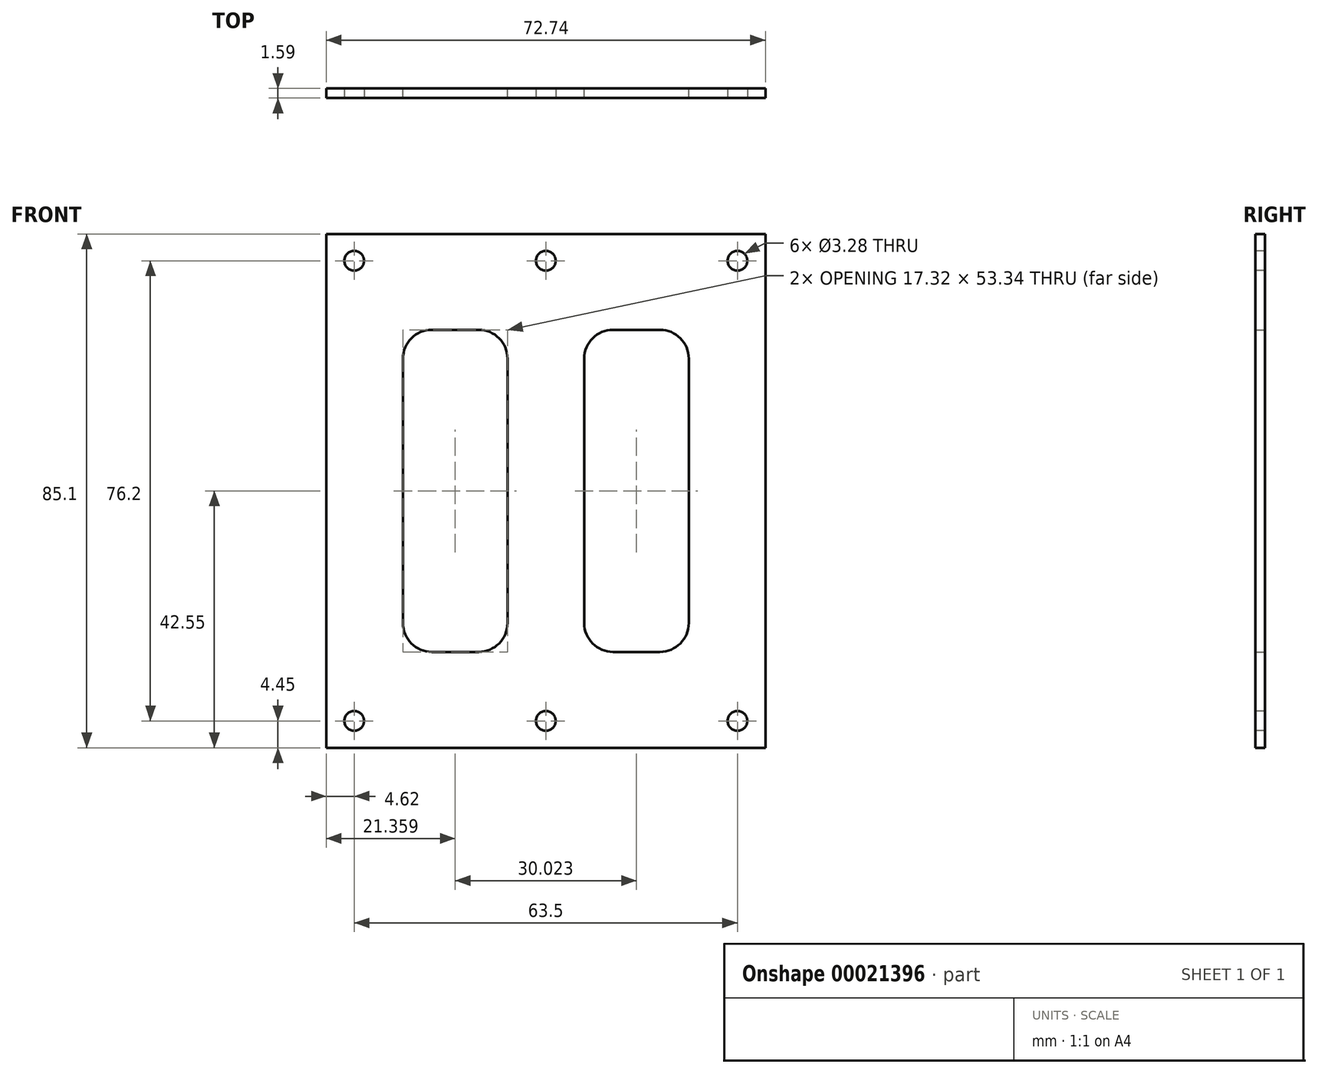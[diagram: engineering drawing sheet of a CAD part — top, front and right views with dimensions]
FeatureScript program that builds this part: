
annotation { "Feature Type Name" : "Feature", "Feature Type Description" : "" }
export const myFeature = defineFeature(function(context is Context, id is Id, definition is map)
    precondition{}
    {
        {
            var Q0;
            Q0=qCreatedBy(makeId("Front.planeOp"),FACE);
            var sketch = newSketch(context, id + "F0", { "sketchPlane" : qUnion([Q0])});
            skLineSegment(sketch, "E0.rect.bottom", {"start": v(-36.37, 42.55) * mm, "end": v(36.37, 42.55) * mm});
            skLineSegment(sketch, "E0.rect.top", {"start": v(-36.37, -42.55) * mm, "end": v(36.37, -42.55) * mm});
            skLineSegment(sketch, "E0.rect.left", {"start": v(-36.37, 42.55) * mm, "end": v(-36.37, -42.55) * mm});
            skLineSegment(sketch, "E0.rect.right", {"start": v(36.37, 42.55) * mm, "end": v(36.37, -42.55) * mm});
            skPoint(sketch, "E0.rect.middle", {"position": v(0, 0) * mm});
            skLineSegment(sketch, "E1.bottom", {"start": v(-23.67, 26.67) * mm, "end": v(-6.35, 26.67) * mm});
            skLineSegment(sketch, "E1.top", {"start": v(-23.67, -26.67) * mm, "end": v(-6.35, -26.67) * mm});
            skLineSegment(sketch, "E1.left", {"start": v(-23.67, 26.67) * mm, "end": v(-23.67, -26.67) * mm});
            skLineSegment(sketch, "E1.right", {"start": v(-6.35, 26.67) * mm, "end": v(-6.35, -26.67) * mm});
            skLineSegment(sketch, "E2.bottom", {"start": v(6.35, 26.67) * mm, "end": v(23.67, 26.67) * mm});
            skLineSegment(sketch, "E2.top", {"start": v(6.35, -26.67) * mm, "end": v(23.67, -26.67) * mm});
            skLineSegment(sketch, "E2.left", {"start": v(6.35, 26.67) * mm, "end": v(6.35, -26.67) * mm});
            skLineSegment(sketch, "E2.right", {"start": v(23.67, 26.67) * mm, "end": v(23.67, -26.67) * mm});
            skLineSegment(sketch, "E3", {"start": v(0, 0) * mm, "end": v(0, 61.31) * mm});
            skLineSegment(sketch, "E4", {"start": v(0, 0) * mm, "end": v(46.15, 0) * mm});
            skSolve(sketch);
        }
        {
            var Q0;
            {var subQ12=sQuery(id+"F0.wireOp",EDGE,"E0.rect.top");Q0=makeQuery(id+"F0.imprint","IMPRINT",FACE,{"disambiguationData":[TD([[makeQuery(id+"F0.imprint","IMPRINT",EDGE,{"derivedFrom":subQ12}),1.0]])]});}
            var Q1;
            {var subQ7=sQuery(id+"F0.wireOp",EDGE,"E2.bottom");Q1=makeQuery(id+"F0.imprint","IMPRINT",FACE,{"disambiguationData":[TD([[makeQuery(id+"F0.imprint","IMPRINT",EDGE,{"derivedFrom":subQ7}),1.0]])]});}
            extrude(context, id + "F1", {"entities" : qUnion([Q0, Q1]), "depth" : 1.59 * mm});
        }
        {
            var Q0;
            Q0=makeQuery(id+"F1.opExtrude","SWEPT_EDGE",EDGE,{"disambiguationData":[OSD([sQuery(id+"F0.wireOp",EDGE,"E2.bottom"),sQuery(id+"F0.wireOp",EDGE,"E2.right")])]});
            var Q1;
            Q1=makeQuery(id+"F1.opExtrude","SWEPT_EDGE",EDGE,{"disambiguationData":[OSD([sQuery(id+"F0.wireOp",EDGE,"E1.bottom"),sQuery(id+"F0.wireOp",EDGE,"E1.right")])]});
            var Q2;
            Q2=makeQuery(id+"F1.opExtrude","SWEPT_EDGE",EDGE,{"disambiguationData":[OSD([sQuery(id+"F0.wireOp",EDGE,"E2.bottom"),sQuery(id+"F0.wireOp",EDGE,"E2.left")])]});
            var Q3;
            Q3=makeQuery(id+"F1.opExtrude","SWEPT_EDGE",EDGE,{"disambiguationData":[OSD([sQuery(id+"F0.wireOp",EDGE,"E1.bottom"),sQuery(id+"F0.wireOp",EDGE,"E1.left")])]});
            var Q4;
            Q4=makeQuery(id+"F1.opExtrude","SWEPT_EDGE",EDGE,{"disambiguationData":[OSD([sQuery(id+"F0.wireOp",EDGE,"E2.top"),sQuery(id+"F0.wireOp",EDGE,"E2.right")])]});
            var Q5;
            Q5=makeQuery(id+"F1.opExtrude","SWEPT_EDGE",EDGE,{"disambiguationData":[OSD([sQuery(id+"F0.wireOp",EDGE,"E1.top"),sQuery(id+"F0.wireOp",EDGE,"E1.right")])]});
            var Q6;
            Q6=makeQuery(id+"F1.opExtrude","SWEPT_EDGE",EDGE,{"disambiguationData":[OSD([sQuery(id+"F0.wireOp",EDGE,"E2.top"),sQuery(id+"F0.wireOp",EDGE,"E2.left")])]});
            var Q7;
            Q7=makeQuery(id+"F1.opExtrude","SWEPT_EDGE",EDGE,{"disambiguationData":[OSD([sQuery(id+"F0.wireOp",EDGE,"E1.top"),sQuery(id+"F0.wireOp",EDGE,"E1.left")])]});
            fillet(context, id + "F2", {"entities" : qUnion([Q0, Q1, Q2, Q3, Q4, Q5, Q6, Q7]), "radius" : 4.78 * mm, "tangentPropagation" : true, "allowEdgeOverflow" : false});
        }
        {
            var Q0;
            Q0=makeQuery(id+"F1.opExtrude","CAP_FACE",FACE,{"disambiguationData":[OSD([sQuery(id+"F0.wireOp",EDGE,"E0.rect.bottom"),sQuery(id+"F0.wireOp",EDGE,"E0.rect.top"),sQuery(id+"F0.wireOp",EDGE,"E0.rect.left"),sQuery(id+"F0.wireOp",EDGE,"E0.rect.right"),sQuery(id+"F0.wireOp",EDGE,"E1.bottom"),sQuery(id+"F0.wireOp",EDGE,"E1.top"),sQuery(id+"F0.wireOp",EDGE,"E1.left"),sQuery(id+"F0.wireOp",EDGE,"E1.right"),sQuery(id+"F0.wireOp",EDGE,"E2.bottom"),sQuery(id+"F0.wireOp",EDGE,"E2.top"),sQuery(id+"F0.wireOp",EDGE,"E2.left"),sQuery(id+"F0.wireOp",EDGE,"E2.right")])],"isStart":false});
            var sketch = newSketch(context, id + "F3", { "sketchPlane" : qUnion([Q0])});
            skLineSegment(sketch, "E5.rect.bottom", {"start": v(31.75, 38.1) * mm, "end": v(-31.75, 38.1) * mm});
            skLineSegment(sketch, "E5.rect.top", {"start": v(31.75, -38.1) * mm, "end": v(-31.75, -38.1) * mm});
            skLineSegment(sketch, "E5.rect.left", {"start": v(31.75, 38.1) * mm, "end": v(31.75, -38.1) * mm});
            skLineSegment(sketch, "E5.rect.right", {"start": v(-31.75, 38.1) * mm, "end": v(-31.75, -38.1) * mm});
            skPoint(sketch, "E5.rect.middle", {"position": v(0, 0) * mm});
            skLineSegment(sketch, "E6", {"start": v(0, 38.1) * mm, "end": v(0, -38.1) * mm});
            skSolve(sketch);
        }
        {
            var Q0;
            Q0=sQuery(id+"F3.wireOp",VERTEX,"E5.rect.right.start");
            var Q1;
            Q1=sQuery(id+"F3.wireOp",VERTEX,"E6.start");
            var Q2;
            Q2=sQuery(id+"F3.wireOp",VERTEX,"E5.rect.bottom.start");
            var Q3;
            Q3=sQuery(id+"F3.wireOp",VERTEX,"E5.rect.left.end");
            var Q4;
            Q4=sQuery(id+"F3.wireOp",VERTEX,"E6.end");
            var Q5;
            Q5=sQuery(id+"F3.wireOp",VERTEX,"E5.rect.right.end");
            var Q6;
            Q6=makeQuery(id+"F1.opExtrude","SWEPT_BODY",BODY,{"disambiguationData":[OSD([sQuery(id+"F0.wireOp",EDGE,"E0.rect.bottom"),sQuery(id+"F0.wireOp",EDGE,"E0.rect.top"),sQuery(id+"F0.wireOp",EDGE,"E0.rect.left"),sQuery(id+"F0.wireOp",EDGE,"E0.rect.right"),sQuery(id+"F0.wireOp",EDGE,"E1.bottom"),sQuery(id+"F0.wireOp",EDGE,"E1.top"),sQuery(id+"F0.wireOp",EDGE,"E1.left"),sQuery(id+"F0.wireOp",EDGE,"E1.right"),sQuery(id+"F0.wireOp",EDGE,"E2.bottom"),sQuery(id+"F0.wireOp",EDGE,"E2.top"),sQuery(id+"F0.wireOp",EDGE,"E2.left"),sQuery(id+"F0.wireOp",EDGE,"E2.right")])]});
            hole(context, id + "F4", {"style" : HoleStyle.SIMPLE, "holeDiameter" : 3.28 * mm, "endStyle" : HoleEndStyle.THROUGH, "locations" : qUnion([Q0, Q1, Q2, Q3, Q4, Q5]), "scope" : qUnion([Q6])});
        }
    });
